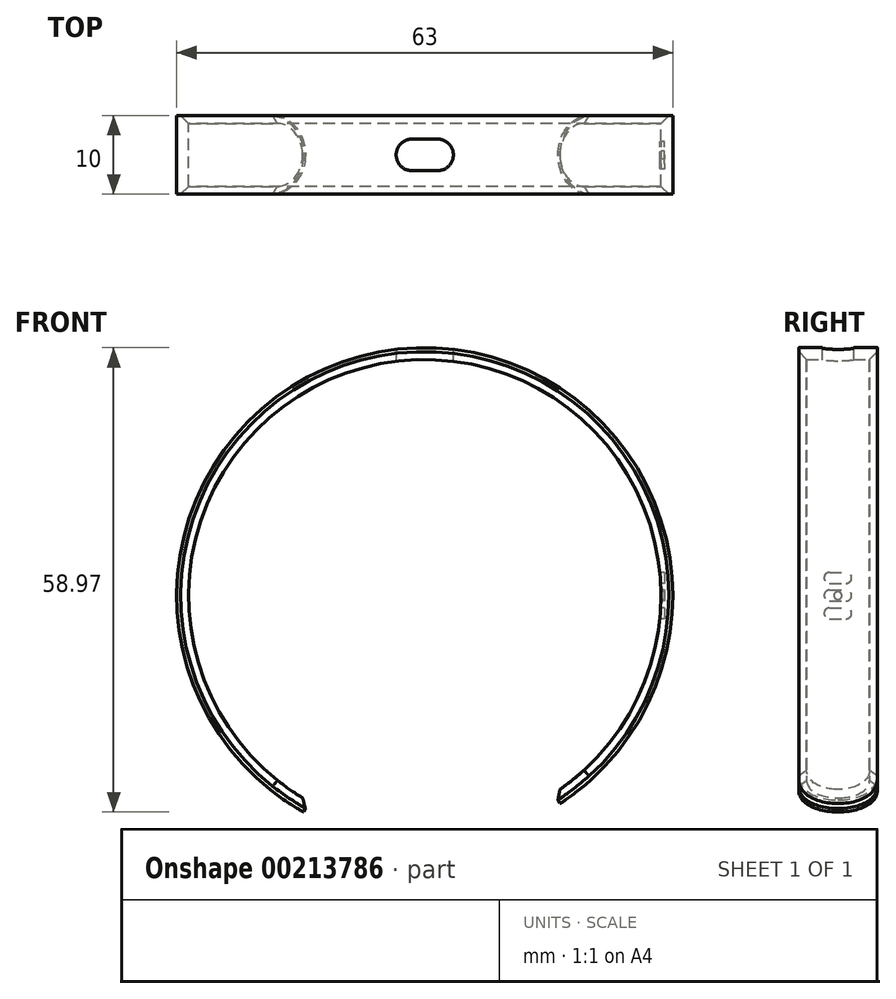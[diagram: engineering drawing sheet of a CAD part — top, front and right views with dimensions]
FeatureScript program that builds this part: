
annotation { "Feature Type Name" : "Feature", "Feature Type Description" : "" }
export const myFeature = defineFeature(function(context is Context, id is Id, definition is map)
    precondition{}
    {
        {
            var Q0;
            Q0=qCreatedBy(makeId("Front.planeOp"),FACE);
            var sketch = newSketch(context, id + "F0", { "sketchPlane" : qUnion([Q0])});
            skCircle(sketch, "E0", {"center": v(0, 0) * mm, "radius": 30 * mm});
            skCircle(sketch, "E1.0", {"center": v(0, 0) * mm, "radius": 31.5 * mm});
            skLineSegment(sketch, "E2.bottom", {"start": v(3.63, 31.29) * mm, "end": v(-3.63, 31.29) * mm, "construction": true});
            skLineSegment(sketch, "E2.top", {"start": v(3.63, 33.45) * mm, "end": v(-3.63, 33.45) * mm});
            skLineSegment(sketch, "E2.left", {"start": v(3.63, 31.29) * mm, "end": v(3.63, 33.45) * mm});
            skLineSegment(sketch, "E2.right", {"start": v(-3.63, 31.29) * mm, "end": v(-3.63, 33.45) * mm});
            skPoint(sketch, "E2.middle", {"position": v(0, 32.37) * mm});
            skLineSegment(sketch, "E3.1.0", {"start": v(-25.28, -18.8) * mm, "end": v(-27.15, -19.87) * mm});
            skLineSegment(sketch, "E3.1.1", {"start": v(-28.91, -12.5) * mm, "end": v(-30.78, -13.58) * mm});
            skLineSegment(sketch, "E3.1.2", {"start": v(-30.78, -13.58) * mm, "end": v(-27.15, -19.87) * mm});
            skLineSegment(sketch, "E3.1.3", {"start": v(-28.91, -12.5) * mm, "end": v(-25.28, -18.8) * mm, "construction": true});
            skLineSegment(sketch, "E3.2.0", {"start": v(28.91, -12.5) * mm, "end": v(30.78, -13.58) * mm});
            skLineSegment(sketch, "E3.2.1", {"start": v(25.28, -18.8) * mm, "end": v(27.15, -19.87) * mm});
            skLineSegment(sketch, "E3.2.2", {"start": v(27.15, -19.87) * mm, "end": v(30.78, -13.58) * mm});
            skLineSegment(sketch, "E3.2.3", {"start": v(25.28, -18.8) * mm, "end": v(28.91, -12.5) * mm, "construction": true});
            skLineSegment(sketch, "E4", {"start": v(0, 0) * mm, "end": v(22.27, 22.27) * mm, "construction": true});
            skLineSegment(sketch, "E5", {"start": v(0, 0) * mm, "end": v(-22.27, 22.27) * mm, "construction": true});
            skLineSegment(sketch, "E6.MirrorCS", {"start": v(0, 0) * mm, "end": v(22.27, -22.27) * mm, "construction": true});
            skLineSegment(sketch, "E7.MirrorCS", {"start": v(0, 0) * mm, "end": v(-22.27, -22.27) * mm, "construction": true});
            skLineSegment(sketch, "E8.0", {"start": v(-0.14, 0.14) * mm, "end": v(0, 0.28) * mm});
            skLineSegment(sketch, "E9.MirrorCS", {"start": v(0.14, -0.14) * mm, "end": v(0.28, 0) * mm});
            skLineSegment(sketch, "E10.MirrorCS", {"start": v(0.14, 0.14) * mm, "end": v(0, 0.28) * mm});
            skLineSegment(sketch, "E11.MirrorCS", {"start": v(-0.14, -0.14) * mm, "end": v(-0.28, 0) * mm});
            skLineSegment(sketch, "E12.MirrorCS", {"start": v(0.14, 0.14) * mm, "end": v(0.28, 0) * mm});
            skLineSegment(sketch, "E13.MirrorCS", {"start": v(-0.14, -0.14) * mm, "end": v(0, -0.28) * mm});
            skLineSegment(sketch, "E14.MirrorCS", {"start": v(0.14, -0.14) * mm, "end": v(0, -0.28) * mm});
            skLineSegment(sketch, "E15.MirrorCS", {"start": v(-0.14, 0.14) * mm, "end": v(-0.28, 0) * mm});
            skLineSegment(sketch, "E16.trimOffspring", {"start": v(-7.2, -7.48) * mm, "end": v(-21.07, -21.35) * mm, "construction": true});
            skLineSegment(sketch, "E17.trimOffspring", {"start": v(-7.48, -7.2) * mm, "end": v(-21.35, -21.07) * mm, "construction": true});
            skLineSegment(sketch, "E18.trimOffspring", {"start": v(-7.48, 7.2) * mm, "end": v(-21.35, 21.07) * mm, "construction": true});
            skLineSegment(sketch, "E19.trimOffspring", {"start": v(-7.2, 7.48) * mm, "end": v(-21.07, 21.35) * mm, "construction": true});
            skLineSegment(sketch, "E20.trimOffspring", {"start": v(7.2, 7.48) * mm, "end": v(21.07, 21.35) * mm, "construction": true});
            skLineSegment(sketch, "E21.trimOffspring", {"start": v(7.48, 7.2) * mm, "end": v(21.35, 21.07) * mm, "construction": true});
            skLineSegment(sketch, "E22.trimOffspring", {"start": v(7.2, -7.48) * mm, "end": v(21.07, -21.35) * mm, "construction": true});
            skLineSegment(sketch, "E23.trimOffspring", {"start": v(7.48, -7.2) * mm, "end": v(21.35, -21.07) * mm, "construction": true});
            skLineSegment(sketch, "E24", {"start": v(-3.63, 31.29) * mm, "end": v(-3.63, 28.18) * mm});
            skLineSegment(sketch, "E25", {"start": v(-3.63, 28.18) * mm, "end": v(3.63, 28.18) * mm});
            skLineSegment(sketch, "E26", {"start": v(3.63, 28.18) * mm, "end": v(3.63, 31.29) * mm});
            skLineSegment(sketch, "E27", {"start": v(28.91, -12.5) * mm, "end": v(7.27, 0) * mm});
            skLineSegment(sketch, "E28", {"start": v(25.28, -18.8) * mm, "end": v(3.35, -6.13) * mm});
            skLineSegment(sketch, "E29", {"start": v(3.35, -6.13) * mm, "end": v(7.27, 0) * mm});
            skLineSegment(sketch, "E30", {"start": v(-25.28, -18.8) * mm, "end": v(-3.28, -6.1) * mm});
            skLineSegment(sketch, "E31", {"start": v(-28.91, -12.5) * mm, "end": v(-6.86, 0.24) * mm});
            skLineSegment(sketch, "E32", {"start": v(-6.86, 0.24) * mm, "end": v(-3.28, -6.1) * mm});
            skLineSegment(sketch, "E33", {"start": v(0, 0.28) * mm, "end": v(1.04, -31.48) * mm, "construction": true});
            skLineSegment(sketch, "E34", {"start": v(0, -0.28) * mm, "end": v(19.14, -25.02) * mm});
            skLineSegment(sketch, "E35.MirrorCS", {"start": v(0.04, -0.28) * mm, "end": v(-17.45, -26.21) * mm});
            skLineSegment(sketch, "E36", {"start": v(0, 0) * mm, "end": v(-15.42, -27.47) * mm});
            skLineSegment(sketch, "E37.MirrorCS", {"start": v(0.02, 0) * mm, "end": v(17.2, -26.4) * mm});
            skSolve(sketch);
        }
        {
            var Q0;
            {var subQ0=sQuery(id+"F0.wireOp",EDGE,"E28");var subQ1=sQuery(id+"F0.wireOp",EDGE,"E0");var subQ2=makeQuery(id+"F0.imprint","INTERSECT",VERTEX,{"derivedFrom":[subQ1,subQ0]});Q0=makeQuery(id+"F0.imprint","IMPRINT",FACE,{"disambiguationData":[TD([[makeQuery(id+"F0.imprint","IMPRINT",EDGE,{"disambiguationData":[TD([[subQ2,-1.0]])],"derivedFrom":subQ1}),-1.0]])]});}
            var Q1;
            {var subQ0=sQuery(id+"F0.wireOp",EDGE,"E26");var subQ1=sQuery(id+"F0.wireOp",EDGE,"E0");var subQ2=makeQuery(id+"F0.imprint","INTERSECT",VERTEX,{"derivedFrom":[subQ1,subQ0]});Q1=makeQuery(id+"F0.imprint","IMPRINT",FACE,{"disambiguationData":[TD([[makeQuery(id+"F0.imprint","IMPRINT",EDGE,{"disambiguationData":[TD([[subQ2,1.0]])],"derivedFrom":subQ1}),-1.0]])]});}
            var Q2;
            {var subQ0=sQuery(id+"F0.wireOp",EDGE,"E24");var subQ1=sQuery(id+"F0.wireOp",EDGE,"E0");var subQ2=makeQuery(id+"F0.imprint","INTERSECT",VERTEX,{"derivedFrom":[subQ1,subQ0]});Q2=makeQuery(id+"F0.imprint","IMPRINT",FACE,{"disambiguationData":[TD([[makeQuery(id+"F0.imprint","IMPRINT",EDGE,{"disambiguationData":[TD([[subQ2,1.0]])],"derivedFrom":subQ1}),-1.0]])]});}
            var Q3;
            {var subQ0=sQuery(id+"F0.wireOp",EDGE,"E24");var subQ1=sQuery(id+"F0.wireOp",EDGE,"E0");var subQ2=makeQuery(id+"F0.imprint","INTERSECT",VERTEX,{"derivedFrom":[subQ1,subQ0]});Q3=makeQuery(id+"F0.imprint","IMPRINT",FACE,{"disambiguationData":[TD([[makeQuery(id+"F0.imprint","IMPRINT",EDGE,{"disambiguationData":[TD([[subQ2,-1.0]])],"derivedFrom":subQ1}),-1.0]])]});}
            var Q4;
            {var subQ0=sQuery(id+"F0.wireOp",EDGE,"E31");var subQ1=sQuery(id+"F0.wireOp",EDGE,"E0");var subQ2=makeQuery(id+"F0.imprint","INTERSECT",VERTEX,{"derivedFrom":[subQ1,subQ0]});Q4=makeQuery(id+"F0.imprint","IMPRINT",FACE,{"disambiguationData":[TD([[makeQuery(id+"F0.imprint","IMPRINT",EDGE,{"disambiguationData":[TD([[subQ2,-1.0]])],"derivedFrom":subQ1}),-1.0]])]});}
            var Q5;
            {var subQ3=sQuery(id+"F0.wireOp",EDGE,"E0");var subQ5=makeQuery(id+"F0.imprint","INTERSECT",VERTEX,{"derivedFrom":[subQ3,sQuery(id+"F0.wireOp",EDGE,"E35.MirrorCS")]});Q5=makeQuery(id+"F0.imprint","IMPRINT",FACE,{"disambiguationData":[TD([[makeQuery(id+"F0.imprint","IMPRINT",EDGE,{"disambiguationData":[TD([[subQ5,1.0]])],"derivedFrom":subQ3}),-1.0]])]});}
            var Q6;
            {var subQ0=sQuery(id+"F0.wireOp",EDGE,"E37.MirrorCS");var subQ1=sQuery(id+"F0.wireOp",EDGE,"E0");var subQ2=makeQuery(id+"F0.imprint","INTERSECT",VERTEX,{"derivedFrom":[subQ1,subQ0]});Q6=makeQuery(id+"F0.imprint","IMPRINT",FACE,{"disambiguationData":[TD([[makeQuery(id+"F0.imprint","IMPRINT",EDGE,{"disambiguationData":[TD([[subQ2,-1.0]])],"derivedFrom":subQ1}),-1.0]])]});}
            var Q7;
            {var subQ0=sQuery(id+"F0.wireOp",EDGE,"E34");var subQ1=sQuery(id+"F0.wireOp",EDGE,"E0");var subQ2=makeQuery(id+"F0.imprint","INTERSECT",VERTEX,{"derivedFrom":[subQ1,subQ0]});Q7=makeQuery(id+"F0.imprint","IMPRINT",FACE,{"disambiguationData":[TD([[makeQuery(id+"F0.imprint","IMPRINT",EDGE,{"disambiguationData":[TD([[subQ2,-1.0]])],"derivedFrom":subQ1}),-1.0]])]});}
            extrude(context, id + "F1", {"entities" : qUnion([Q0, Q1, Q2, Q3, Q4, Q5, Q6, Q7]), "depth" : 5 * mm, "hasSecondDirection" : true, "secondDirectionOppositeDirection" : true, "secondDirectionDepth" : 5 * mm});
        }
        {
            var Q0;
            Q0=qCreatedBy(makeId("Top.planeOp"),FACE);
            var sketch = newSketch(context, id + "F2", { "sketchPlane" : qUnion([Q0])});
            skCircle(sketch, "E38", {"center": v(0, 0) * mm, "radius": 0.15 * mm});
            skCircle(sketch, "E39.1.0.0", {"center": v(0, -0.6) * mm, "radius": 0.15 * mm});
            skCircle(sketch, "E39.2.0.0", {"center": v(0, -1.2) * mm, "radius": 0.15 * mm});
            skCircle(sketch, "E39.3.0.0", {"center": v(0, -1.8) * mm, "radius": 0.15 * mm});
            skCircle(sketch, "E39.4.0.0", {"center": v(0, -2.4) * mm, "radius": 0.15 * mm});
            skCircle(sketch, "E39.5.0.0", {"center": v(0, -3) * mm, "radius": 0.15 * mm});
            skCircle(sketch, "E39.6.0.0", {"center": v(0, -3.6) * mm, "radius": 0.15 * mm});
            skLineSegment(sketch, "E39.direction1", {"start": v(0, 0) * mm, "end": v(0, -0.6) * mm, "construction": true});
            skCircle(sketch, "E40.MirrorC", {"center": v(0, 0.6) * mm, "radius": 0.15 * mm});
            skCircle(sketch, "E41.MirrorC", {"center": v(0, 1.2) * mm, "radius": 0.15 * mm});
            skCircle(sketch, "E42.MirrorC", {"center": v(0, 1.8) * mm, "radius": 0.15 * mm});
            skCircle(sketch, "E43.MirrorC", {"center": v(0, 2.4) * mm, "radius": 0.15 * mm});
            skCircle(sketch, "E44.MirrorC", {"center": v(0, 3) * mm, "radius": 0.15 * mm});
            skCircle(sketch, "E45.MirrorC", {"center": v(0, 3.6) * mm, "radius": 0.15 * mm});
            skSolve(sketch);
        }
        {
            var Q0;
            Q0=makeQuery(id+"F0.imprint","IMPRINT",FACE,{"disambiguationData":[TD([[makeQuery(id+"F0.imprint","IMPRINT",EDGE,{"derivedFrom":sQuery(id+"F0.wireOp",EDGE,"E2.top")}),1.0]])]});
            var Q1;
            {var subQ0=sQuery(id+"F0.wireOp",EDGE,"E24");var subQ1=sQuery(id+"F0.wireOp",EDGE,"E0");var subQ2=makeQuery(id+"F0.imprint","INTERSECT",VERTEX,{"derivedFrom":[subQ1,subQ0]});Q1=makeQuery(id+"F0.imprint","IMPRINT",FACE,{"disambiguationData":[TD([[makeQuery(id+"F0.imprint","IMPRINT",EDGE,{"disambiguationData":[TD([[subQ2,1.0]])],"derivedFrom":subQ1}),-1.0]])]});}
            var Q2;
            {var subQ5=sQuery(id+"F0.wireOp",EDGE,"E25");Q2=makeQuery(id+"F0.imprint","IMPRINT",FACE,{"disambiguationData":[TD([[makeQuery(id+"F0.imprint","IMPRINT",EDGE,{"derivedFrom":subQ5}),1.0]])]});}
            extrude(context, id + "F3", {"entities" : qUnion([Q0, Q1, Q2]), "operationType" : NewBodyOperationType.REMOVE, "flatOperationType" : FlatOperationType.REMOVE, "oppositeDirection" : true, "offsetDistance" : 25 * mm, "depth" : 2 * mm, "hasSecondDirection" : true, "secondDirectionOppositeDirection" : false, "secondDirectionDepth" : 2 * mm, "domain" : OperationDomain.MODEL});
        }
        {
            var Q0;
            Q0=makeQuery(id+"F1.opExtrude","CAP_EDGE",EDGE,{"disambiguationData":[OSD([sQuery(id+"F0.wireOp",EDGE,"E34")])],"isStart":false});
            var Q1;
            Q1=makeQuery(id+"F1.opExtrude","CAP_EDGE",EDGE,{"disambiguationData":[OSD([sQuery(id+"F0.wireOp",EDGE,"E34")])],"isStart":true});
            var Q2;
            Q2=makeQuery(id+"F1.opExtrude","CAP_EDGE",EDGE,{"disambiguationData":[OSD([sQuery(id+"F0.wireOp",EDGE,"E30")])],"isStart":true});
            var Q3;
            Q3=makeQuery(id+"F1.opExtrude","CAP_EDGE",EDGE,{"disambiguationData":[OSD([sQuery(id+"F0.wireOp",EDGE,"E30")])],"isStart":false});
            var Q4;
            Q4=makeQuery(id+"F1.opExtrude","CAP_EDGE",EDGE,{"disambiguationData":[OSD([sQuery(id+"F0.wireOp",EDGE,"E28")])],"isStart":false});
            var Q5;
            Q5=makeQuery(id+"F1.opExtrude","CAP_EDGE",EDGE,{"disambiguationData":[OSD([sQuery(id+"F0.wireOp",EDGE,"E28")])],"isStart":true});
            var Q6;
            Q6=makeQuery(id+"F1.opExtrude","CAP_EDGE",EDGE,{"disambiguationData":[OSD([sQuery(id+"F0.wireOp",EDGE,"E36")])],"isStart":true});
            var Q7;
            Q7=makeQuery(id+"F1.opExtrude","CAP_EDGE",EDGE,{"disambiguationData":[OSD([sQuery(id+"F0.wireOp",EDGE,"E36")])],"isStart":false});
            var Q8;
            Q8=makeQuery(id+"F1.opExtrude","CAP_EDGE",EDGE,{"disambiguationData":[OSD([sQuery(id+"F0.wireOp",EDGE,"E37.MirrorCS")])],"isStart":false});
            var Q9;
            Q9=makeQuery(id+"F1.opExtrude","CAP_EDGE",EDGE,{"disambiguationData":[OSD([sQuery(id+"F0.wireOp",EDGE,"E37.MirrorCS")])],"isStart":true});
            fillet(context, id + "F4", {"entities" : qUnion([Q0, Q1, Q2, Q3, Q4, Q5, Q6, Q7, Q8, Q9]), "radius" : 5 * mm, "tangentPropagation" : true, "defaultsChanged" : false, "vertexSettings" : [], "allowEdgeOverflow" : false});
        }
        {
            var Q0;
            Q0=makeQuery(id+"F1.opExtrude","CAP_EDGE",EDGE,{"disambiguationData":[OSD([sQuery(id+"F0.wireOp",EDGE,"E0")])],"isStart":true});
            var Q1;
            Q1=makeQuery(id+"F1.opExtrude","CAP_EDGE",EDGE,{"disambiguationData":[OSD([sQuery(id+"F0.wireOp",EDGE,"E0")])],"isStart":false});
            chamfer(context, id + "F5", {"entities" : qUnion([Q0, Q1]), "width" : 1 * mm, "tangentPropagation" : true});
        }
        {
            var Q0;
            Q0=makeQuery(id+"F3.boolean.opBoolean","COPY",EDGE,{"derivedFrom":makeQuery(id+"F3.opExtrude","CAP_EDGE",EDGE,{"disambiguationData":[OSD([sQuery(id+"F0.wireOp",EDGE,"E2.left"),sQuery(id+"F0.wireOp",EDGE,"E26")])],"isStart":false})});
            var Q1;
            Q1=makeQuery(id+"F3.boolean.opBoolean","COPY",EDGE,{"derivedFrom":makeQuery(id+"F3.opExtrude","CAP_EDGE",EDGE,{"disambiguationData":[OSD([sQuery(id+"F0.wireOp",EDGE,"E2.right"),sQuery(id+"F0.wireOp",EDGE,"E24")])],"isStart":false})});
            var Q2;
            Q2=makeQuery(id+"F3.boolean.opBoolean","COPY",EDGE,{"derivedFrom":makeQuery(id+"F3.opExtrude","CAP_EDGE",EDGE,{"disambiguationData":[OSD([sQuery(id+"F0.wireOp",EDGE,"E2.right"),sQuery(id+"F0.wireOp",EDGE,"E24")])],"isStart":true})});
            var Q3;
            Q3=makeQuery(id+"F3.boolean.opBoolean","COPY",EDGE,{"derivedFrom":makeQuery(id+"F3.opExtrude","CAP_EDGE",EDGE,{"disambiguationData":[OSD([sQuery(id+"F0.wireOp",EDGE,"E2.left"),sQuery(id+"F0.wireOp",EDGE,"E26")])],"isStart":true})});
            fillet(context, id + "F6", {"entities" : qUnion([Q0, Q1, Q2, Q3]), "radius" : 2 * mm, "tangentPropagation" : true, "allowEdgeOverflow" : false});
        }
        {
            var Q0;
            Q0=qCreatedBy(makeId("Right.planeOp"),FACE);
            var sketch = newSketch(context, id + "F7", { "sketchPlane" : qUnion([Q0])});
            skLineSegment(sketch, "E46.bottom", {"start": v(-1.07, -0.68) * mm, "end": v(1.02, -0.68) * mm});
            skArc(sketch, "E47.filletArc", {"start": v(-1.07, 0.72) * mm, "mid": v(-1.57, 0.51) * mm, "end": v(-1.77, 0.02) * mm});
            skArc(sketch, "E48.filletArc", {"start": v(-1.77, 0.02) * mm, "mid": v(-1.57, -0.48) * mm, "end": v(-1.07, -0.68) * mm});
            skArc(sketch, "E49.filletArc", {"start": v(1.72, 0.02) * mm, "mid": v(1.52, 0.51) * mm, "end": v(1.02, 0.72) * mm});
            skArc(sketch, "E50.filletArc", {"start": v(1.02, -0.68) * mm, "mid": v(1.52, -0.48) * mm, "end": v(1.72, 0.02) * mm});
            skLineSegment(sketch, "E51.bottom", {"start": v(-1.07, -2.93) * mm, "end": v(1.02, -2.93) * mm});
            skLineSegment(sketch, "E51.top", {"start": v(-1.07, -1.53) * mm, "end": v(1.02, -1.53) * mm});
            skArc(sketch, "E52.filletArc", {"start": v(-1.07, -1.53) * mm, "mid": v(-1.57, -1.74) * mm, "end": v(-1.77, -2.23) * mm});
            skArc(sketch, "E53.filletArc", {"start": v(-1.77, -2.23) * mm, "mid": v(-1.57, -2.73) * mm, "end": v(-1.07, -2.93) * mm});
            skArc(sketch, "E54.filletArc", {"start": v(1.72, -2.23) * mm, "mid": v(1.52, -1.74) * mm, "end": v(1.02, -1.53) * mm});
            skArc(sketch, "E55.filletArc", {"start": v(1.02, -2.93) * mm, "mid": v(1.52, -2.73) * mm, "end": v(1.72, -2.23) * mm});
            skLineSegment(sketch, "E56", {"start": v(-1.07, 0.72) * mm, "end": v(1.02, 0.72) * mm});
            skCircle(sketch, "E57", {"center": v(-0.02, 0.02) * mm, "radius": 0.5 * mm});
            skLineSegment(sketch, "E58.bottom", {"start": v(-1.07, 1.57) * mm, "end": v(1.02, 1.57) * mm});
            skLineSegment(sketch, "E58.top", {"start": v(-1.07, 2.97) * mm, "end": v(1.02, 2.97) * mm});
            skArc(sketch, "E59.filletArc", {"start": v(-1.07, 2.97) * mm, "mid": v(-1.57, 2.77) * mm, "end": v(-1.77, 2.27) * mm});
            skArc(sketch, "E60.filletArc", {"start": v(-1.77, 2.27) * mm, "mid": v(-1.57, 1.78) * mm, "end": v(-1.07, 1.57) * mm});
            skArc(sketch, "E61.filletArc", {"start": v(1.72, 2.27) * mm, "mid": v(1.52, 2.77) * mm, "end": v(1.02, 2.97) * mm});
            skArc(sketch, "E62.filletArc", {"start": v(1.02, 1.57) * mm, "mid": v(1.52, 1.78) * mm, "end": v(1.72, 2.27) * mm});
            skSolve(sketch);
        }
        {
            var Q0;
            Q0=makeQuery(id+"F7.imprint","IMPRINT",FACE,{"disambiguationData":[TD([[makeQuery(id+"F7.imprint","IMPRINT",EDGE,{"derivedFrom":sQuery(id+"F7.wireOp",EDGE,"E58.bottom")}),1.0]])]});
            var Q1;
            Q1=makeQuery(id+"F7.imprint","IMPRINT",FACE,{"disambiguationData":[TD([[makeQuery(id+"F7.imprint","IMPRINT",EDGE,{"derivedFrom":sQuery(id+"F7.wireOp",EDGE,"E46.bottom")}),1.0]])]});
            var Q2;
            Q2=makeQuery(id+"F7.imprint","IMPRINT",FACE,{"disambiguationData":[TD([[makeQuery(id+"F7.imprint","IMPRINT",EDGE,{"derivedFrom":sQuery(id+"F7.wireOp",EDGE,"E51.bottom")}),1.0]])]});
            extrude(context, id + "F8", {"entities" : qUnion([Q0, Q1, Q2]), "operationType" : NewBodyOperationType.REMOVE, "depth" : 30.43 * mm, "offsetDistance" : 25 * mm});
        }
    });
